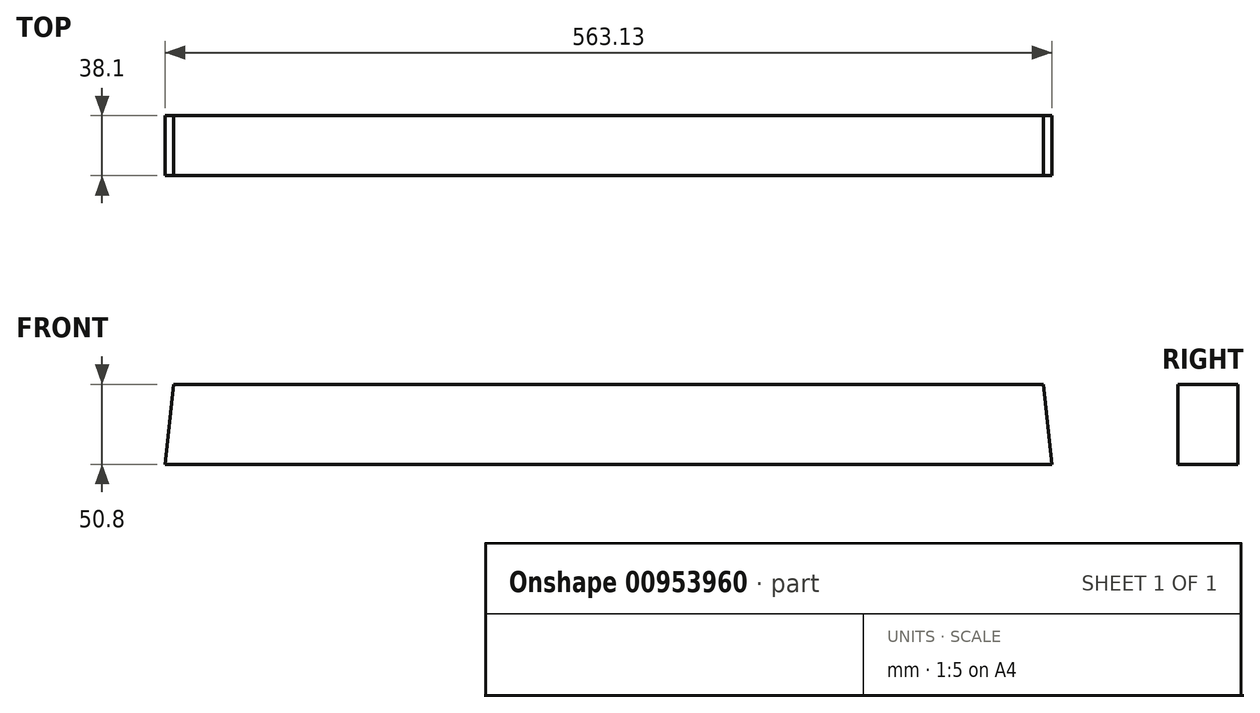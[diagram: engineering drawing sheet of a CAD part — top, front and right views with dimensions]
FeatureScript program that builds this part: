
annotation { "Feature Type Name" : "Feature", "Feature Type Description" : "" }
export const myFeature = defineFeature(function(context is Context, id is Id, definition is map)
    precondition{}
    {
        {
            var Q0;
            Q0=qCreatedBy(makeId("Front.planeOp"),FACE);
            var sketch = newSketch(context, id + "F0", { "sketchPlane" : qUnion([Q0])});
            skLineSegment(sketch, "E0", {"start": v(0, 0) * mm, "end": v(552.45, 0) * mm});
            skLineSegment(sketch, "E1", {"start": v(552.45, 0) * mm, "end": v(557.79, -50.8) * mm});
            skLineSegment(sketch, "E2", {"start": v(557.79, -50.8) * mm, "end": v(-5.34, -50.8) * mm});
            skLineSegment(sketch, "E3", {"start": v(-5.34, -50.8) * mm, "end": v(0, 0) * mm});
            skLineSegment(sketch, "E4", {"start": v(0, 0) * mm, "end": v(0, -50.8) * mm, "construction": true});
            skLineSegment(sketch, "E5", {"start": v(552.45, 0) * mm, "end": v(552.45, -50.8) * mm, "construction": true});
            skSolve(sketch);
        }
        {
            var Q0;
            Q0=makeQuery(id+"F0.imprint","IMPRINT",FACE,{"disambiguationData":[TD([[makeQuery(id+"F0.imprint","IMPRINT",EDGE,{"derivedFrom":sQuery(id+"F0.wireOp",EDGE,"E0")}),-1.0]])]});
            extrude(context, id + "F1", {"entities" : qUnion([Q0]), "depth" : 38.1 * mm, "offsetDistance" : 25.4 * mm});
        }
    });
